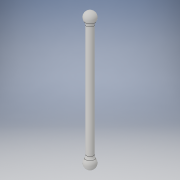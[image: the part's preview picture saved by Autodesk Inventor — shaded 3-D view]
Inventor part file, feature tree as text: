
AUTODESK INVENTOR PART (.ipt)
format: ipt  version: 2018 (Build 220112000, 112)  size: 117,760 bytes
history: native  units: mm
features: revolve x1, sketch x1
ambient origin geometry x8: Origin, YZ Plane, XZ Plane, XY Plane, X Axis, Y Axis, Z Axis, Center Point
bodies: Solid1 (feature_tree)
feature tree (2):
  revolve  "Revolution1"  [1 undecoded]
  sketch  "Sketch1"  dims[d0=5.0mm d1=1.5mm d2=25.75mm d3=2.0mm d4=90.0deg]
note: 1 required parameter value undecoded (feature->parameter linkage not recoverable at this tier; creation-order binding heuristic only, values carry confidence <= 0.55)
